# Revit family: Malvestio_346780H
name_source: partatom
category: Furniture
revit_build: Autodesk Revit Architecture 2014 (Build: 20131024_2115(x64)
units: mm (PartAtom-declared; Revit-internal decimal feet)

## types (1)
- Malvestio_346780H
    BIMobject category = Other Furniture
    Date of publishing = 2014-10-30
    Depth = 840 mm  [stored 2.75591 ft]
    Description = Bed, electric, 4 sections, abs mattress platform, height adjustment with compass movement, translating backrest, electrically adjustable trend/reverse trend, integrated bed lengthener, battery included.
    Design country = Italy
    Edition number = 1
    Height = 800 mm  [stored 2.62467 ft]
    IFC Classification = Furniture
    Installation instructions = http://www.malvestio.it
    Manufacturer country = Italy
    Manufacturer name = Malvestio
    Manufacturer url = http://www.malvestio.it
    Material Secondary = Stainless-Malvestio-346780H-Steel
    Material main = Plastic-Malvestio-346780H-Laminated
    Nominal height = 800
    Nominal width = 2180
    Product SKU = ALL-WARDS-346780H
    Product data url = http://www.malvestio.it
    QR code = http://malvestio.bimobject.com
    UNSPSC Code = 56
    UNSPSC Name = Furniture and Furnishings
    URL = http://malvestio.bimobject.com
    Weight Net (Kg) = 100
    Width = 2180 mm  [stored 7.15223 ft]
    Youtube clip = http://www.malvestio.it

note: [stored X ft] marks values corroborated as IEEE doubles in the binary element streams (Revit-internal decimal feet)

## geometry (parser evidence)
native form markers: Sweep x3
no freeform markers — native parametric forms only
